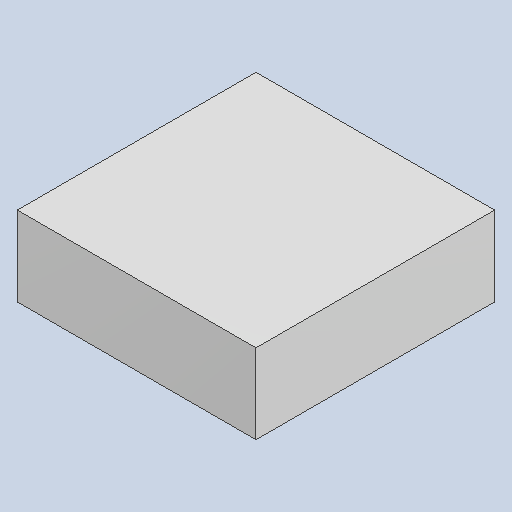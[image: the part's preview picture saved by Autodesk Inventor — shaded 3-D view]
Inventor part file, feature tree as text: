
AUTODESK INVENTOR PART (.ipt)
format: ipt  version: 2023.4 (Build 274418000, 418)  size: 79,872 bytes
history: native  units: mm
features: extrude x1
ambient origin geometry x8: Origin, YZ Plane, XZ Plane, XY Plane, X Axis, Y Axis, Z Axis, Center Point
bodies: Solid1 (feature_tree)
feature tree (1):
  extrude  "Extruded_34"  [1 undecoded]
note: 1 required parameter value undecoded (feature->parameter linkage not recoverable at this tier; creation-order binding heuristic only, values carry confidence <= 0.55)
